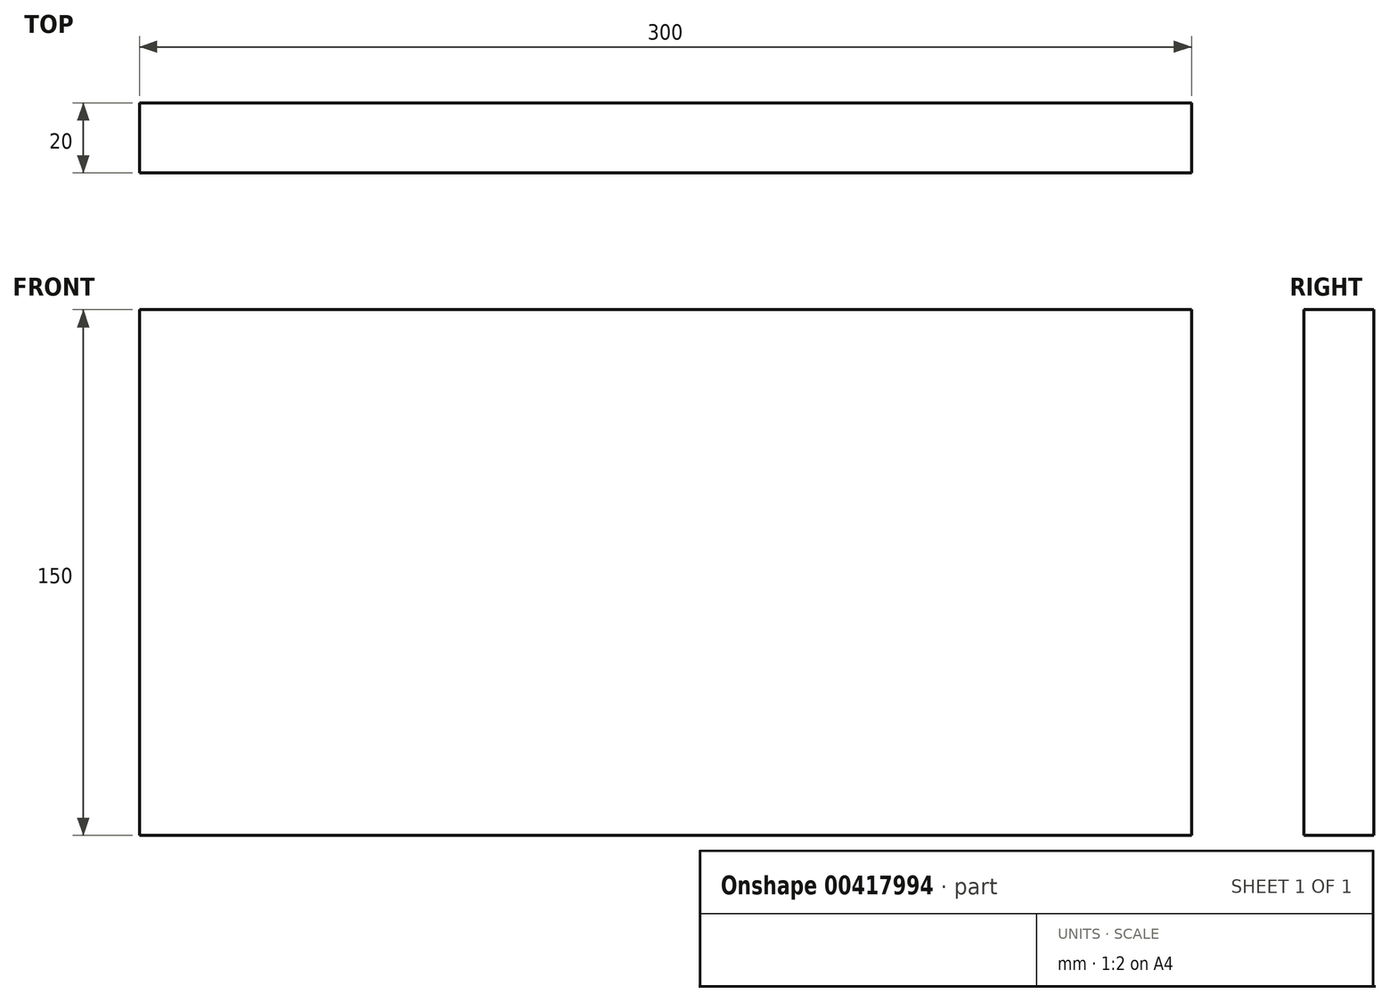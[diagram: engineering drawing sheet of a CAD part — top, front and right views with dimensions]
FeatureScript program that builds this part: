
annotation { "Feature Type Name" : "Feature", "Feature Type Description" : "" }
export const myFeature = defineFeature(function(context is Context, id is Id, definition is map)
    precondition{}
    {
        {
            var Q0;
            Q0=qCreatedBy(makeId("Front.planeOp"),FACE);
            var sketch = newSketch(context, id + "F0", { "sketchPlane" : qUnion([Q0])});
            skLineSegment(sketch, "E0.bottom", {"start": v(150, -75) * mm, "end": v(-150, -75) * mm});
            skLineSegment(sketch, "E0.top", {"start": v(150, 75) * mm, "end": v(-150, 75) * mm});
            skLineSegment(sketch, "E0.left", {"start": v(150, -75) * mm, "end": v(150, 75) * mm});
            skLineSegment(sketch, "E0.right", {"start": v(-150, -75) * mm, "end": v(-150, 75) * mm});
            skPoint(sketch, "E0.middle", {"position": v(0, 0) * mm});
            skSolve(sketch);
        }
        {
            var Q0;
            Q0 = qSketchRegion(id + "F0", true);
            var Q1;
            Q1=makeQuery(id+"F0.imprint","IMPRINT",FACE,{"disambiguationData":[TD([[makeQuery(id+"F0.imprint","IMPRINT",EDGE,{"derivedFrom":sQuery(id+"F0.wireOp",EDGE,"E0.bottom")}),-1.0]])]});
            extrude(context, id + "F1", {"entities" : qUnion([Q0, Q1]), "endBound" : BoundingType.SYMMETRIC, "depth" : 20 * mm});
        }
    });
